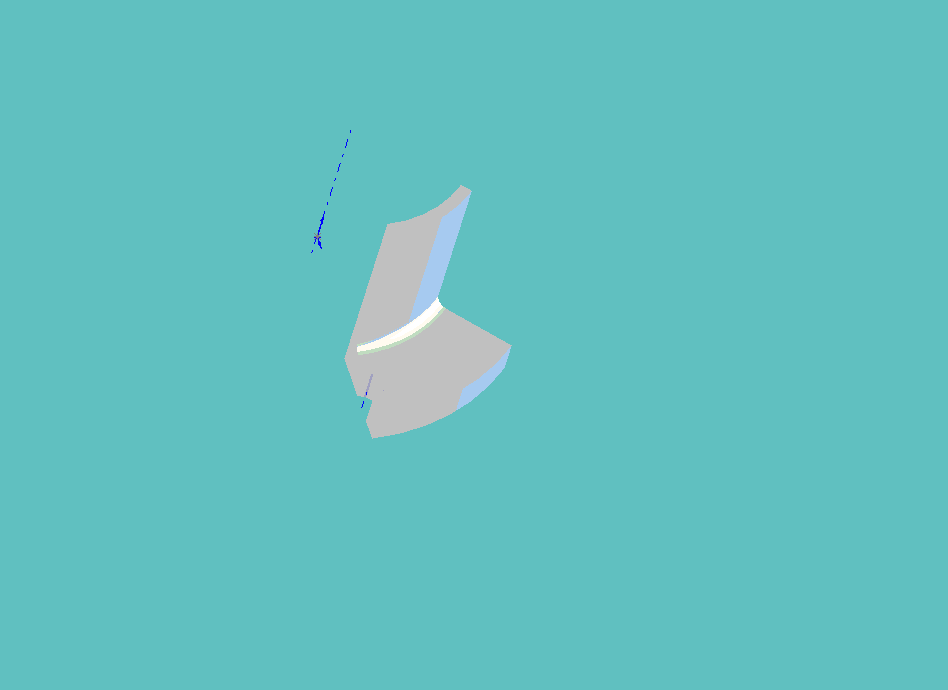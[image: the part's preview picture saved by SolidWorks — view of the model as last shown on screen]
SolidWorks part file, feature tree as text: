
SOLIDWORKS PART (.sldprt)
format: sldprt  version: not decoded by parser v0  size: 118,272 bytes
history: native  units: mm
features: sketch x7, extrude x2, cut_extrude x2, material x1, fillet x1, hole x1, pattern_circular x1 (+11 scaffold rows collapsed)
feature tree (26):
  scaffold x11  (default folders/planes/origin — collapsed)
  material  "Material <not specified>"
  sketch  "Sketch1"  dims[D1=150.0mm]
  extrude  "Extrude1"  Depth=30mm
  sketch  "Sketch2"  dims[D1=~114.862514mm]
  extrude  "Extrude2"  Depth=180mm
  sketch  "Sketch3"  dims[D1=~81.588525mm]
  cut_extrude  "Cut-Extrude1"  [1 undecoded]
  fillet  "Fillet1"  Radius=10mm
  hole  "M25.0 (25) Diameter Hole1"  Diameter=25mm Depth=180mm
  sketch  "Sketch15"  dims[D1=150.0mm]
  sketch  "Sketch14"  dims[hole-wizard template sketch: 59 standard entries collapsed; hole parameters kept: c18.Thru Hole Dia.=25.0mm c18.Thru Hole Depth=180.0mm]
  pattern_circular  "CirPattern3"  Count=4 Angle=360deg
  sketch  "Sketch17"  dims[c1.D1=~221.47651mm c2.D1=45.0deg]
  cut_extrude  "Cut-Extrude2"  [1 undecoded]
  sketch  "Sketch22"  dims[D1=~25.705256mm]
decode coverage: 12 of 14 modeling features carry decoded parameters
note: ~ marks probable driven/reference dimensions
note: 2 parameter values undecoded
note: suppression state not decoded; provenance and decode notes live in map.json
